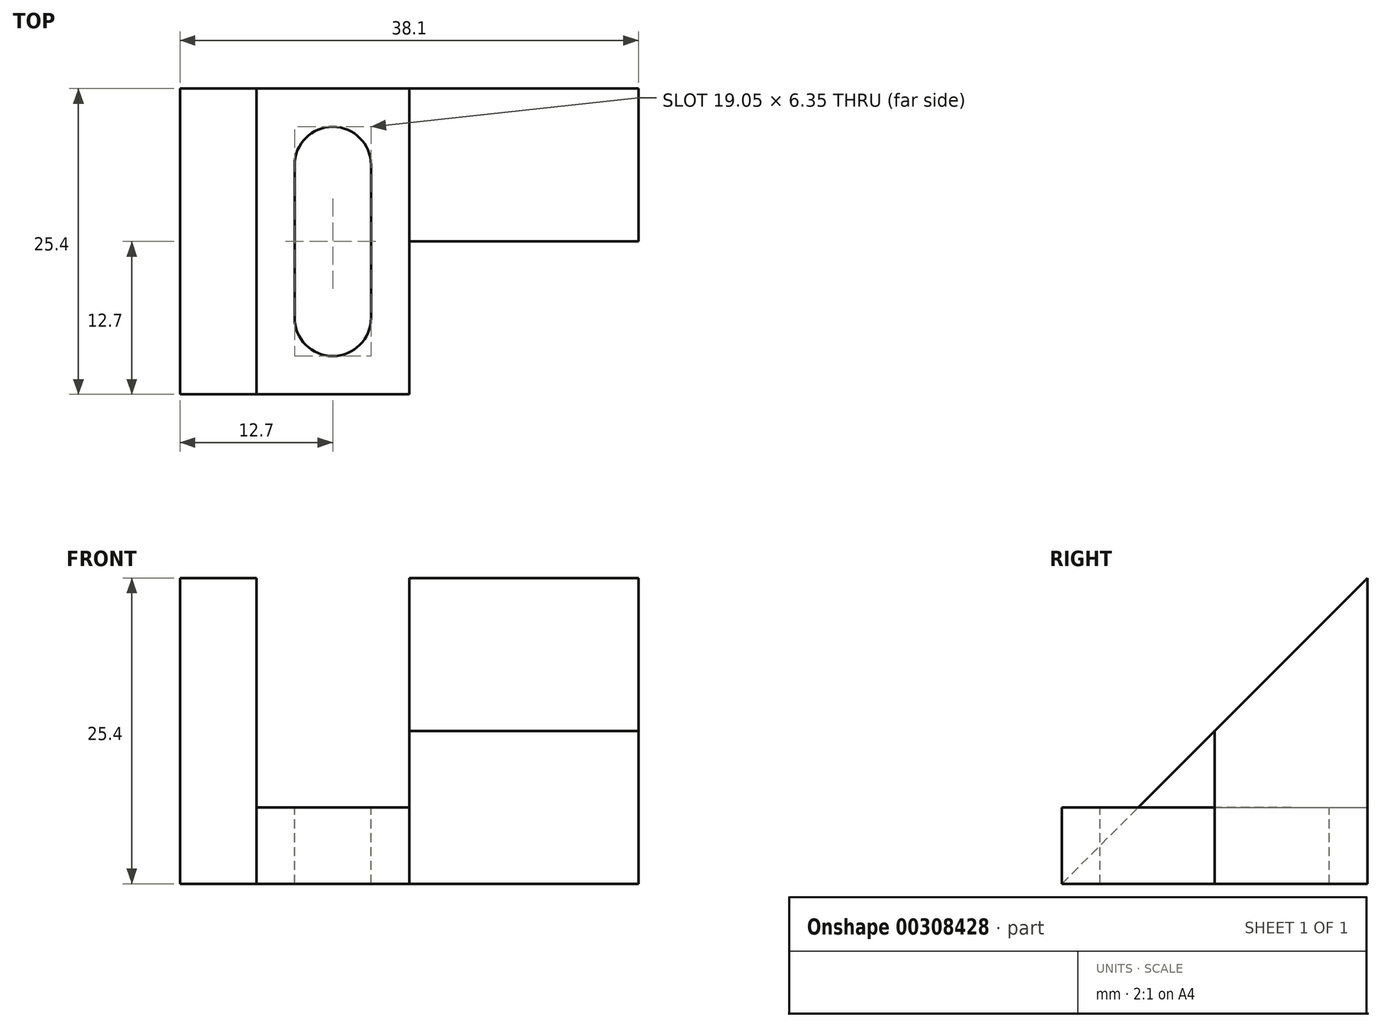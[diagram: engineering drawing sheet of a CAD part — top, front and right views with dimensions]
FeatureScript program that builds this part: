
annotation { "Feature Type Name" : "Feature", "Feature Type Description" : "" }
export const myFeature = defineFeature(function(context is Context, id is Id, definition is map)
    precondition{}
    {
        {
            var Q0;
            Q0=qCreatedBy(makeId("Front.planeOp"),FACE);
            var sketch = newSketch(context, id + "F0", { "sketchPlane" : qUnion([Q0])});
            skLineSegment(sketch, "E0", {"start": v(0, 0) * mm, "end": v(38.1, 0) * mm});
            skLineSegment(sketch, "E1", {"start": v(38.1, 0) * mm, "end": v(38.1, 25.4) * mm});
            skLineSegment(sketch, "E2", {"start": v(38.1, 25.4) * mm, "end": v(19.05, 25.4) * mm});
            skLineSegment(sketch, "E3", {"start": v(19.05, 25.4) * mm, "end": v(19.05, 6.35) * mm});
            skLineSegment(sketch, "E4", {"start": v(19.05, 6.35) * mm, "end": v(6.35, 6.35) * mm});
            skLineSegment(sketch, "E5", {"start": v(6.35, 6.35) * mm, "end": v(6.35, 25.4) * mm});
            skLineSegment(sketch, "E6", {"start": v(6.35, 25.4) * mm, "end": v(0, 25.4) * mm});
            skLineSegment(sketch, "E7", {"start": v(0, 25.4) * mm, "end": v(0, 0) * mm});
            skSolve(sketch);
        }
        {
            var Q0;
            Q0 = qSketchRegion(id + "F0", true);
            extrude(context, id + "F1", {"entities" : qUnion([Q0]), "depth" : 25.4 * mm});
        }
        {
            var Q0;
            Q0=makeQuery(id+"F1.opExtrude","SWEPT_FACE",FACE,{"disambiguationData":[OSD([sQuery(id+"F0.wireOp",EDGE,"E1")])]});
            var sketch = newSketch(context, id + "F2", { "sketchPlane" : qUnion([Q0])});
            skLineSegment(sketch, "E8", {"start": v(-25.4, 0) * mm, "end": v(-12.7, 0) * mm});
            skLineSegment(sketch, "E9", {"start": v(-12.7, 0) * mm, "end": v(-12.7, 25.4) * mm});
            skLineSegment(sketch, "E10", {"start": v(-12.7, 25.4) * mm, "end": v(-25.4, 25.4) * mm});
            skLineSegment(sketch, "E11", {"start": v(-25.4, 25.4) * mm, "end": v(-25.4, 0) * mm});
            skSolve(sketch);
        }
        {
            var Q0;
            Q0 = qSketchRegion(id + "F2", true);
            extrude(context, id + "F3", {"entities" : qUnion([Q0]), "operationType" : NewBodyOperationType.REMOVE, "oppositeDirection" : true, "depth" : 19.05 * mm});
        }
        {
            var Q0;
            Q0=makeQuery(id+"F1.opExtrude","SWEPT_FACE",FACE,{"disambiguationData":[OSD([sQuery(id+"F0.wireOp",EDGE,"E1")])]});
            var sketch = newSketch(context, id + "F4", { "sketchPlane" : qUnion([Q0])});
            skLineSegment(sketch, "E12", {"start": v(-12.7, 12.7) * mm, "end": v(0, 25.4) * mm});
            skLineSegment(sketch, "E13", {"start": v(-12.7, 25.4) * mm, "end": v(-12.7, 12.7) * mm});
            skLineSegment(sketch, "E14", {"start": v(-12.7, 25.4) * mm, "end": v(0, 25.4) * mm});
            skSolve(sketch);
        }
        {
            var Q0;
            Q0 = qSketchRegion(id + "F4", true);
            extrude(context, id + "F5", {"entities" : qUnion([Q0]), "operationType" : NewBodyOperationType.REMOVE, "oppositeDirection" : true, "depth" : 19.05 * mm});
        }
        {
            var Q0;
            Q0=makeQuery(id+"F1.opExtrude","SWEPT_FACE",FACE,{"disambiguationData":[OSD([sQuery(id+"F0.wireOp",EDGE,"E7")])]});
            var sketch = newSketch(context, id + "F6", { "sketchPlane" : qUnion([Q0])});
            skLineSegment(sketch, "E15", {"start": v(0, 25.4) * mm, "end": v(25.4, 25.4) * mm});
            skLineSegment(sketch, "E16", {"start": v(25.4, 25.4) * mm, "end": v(25.4, 0) * mm});
            skLineSegment(sketch, "E17", {"start": v(25.4, 0) * mm, "end": v(0, 25.4) * mm});
            skSolve(sketch);
        }
        {
            var Q0;
            Q0 = qSketchRegion(id + "F6", true);
            extrude(context, id + "F7", {"entities" : qUnion([Q0]), "operationType" : NewBodyOperationType.REMOVE, "oppositeDirection" : true, "depth" : 6.35 * mm});
        }
        {
            var Q0;
            Q0=makeQuery(id+"F1.opExtrude","SWEPT_FACE",FACE,{"disambiguationData":[OSD([sQuery(id+"F0.wireOp",EDGE,"E4")])]});
            var sketch = newSketch(context, id + "F8", { "sketchPlane" : qUnion([Q0])});
            skLineSegment(sketch, "E18", {"start": v(6.35, 0) * mm, "end": v(12.7, 0) * mm});
            skLineSegment(sketch, "E19", {"start": v(12.7, 0) * mm, "end": v(12.7, -6.35) * mm});
            skLineSegment(sketch, "E20", {"start": v(12.7, -25.4) * mm, "end": v(12.7, -19.05) * mm});
            skCircle(sketch, "E21", {"center": v(12.7, -19.05) * mm, "radius": 3.18 * mm});
            skCircle(sketch, "E22", {"center": v(12.7, -6.35) * mm, "radius": 3.18 * mm});
            skLineSegment(sketch, "E23", {"start": v(9.53, -6.35) * mm, "end": v(9.53, -19.05) * mm});
            skLineSegment(sketch, "E24", {"start": v(15.88, -6.35) * mm, "end": v(15.88, -19.05) * mm});
            skSolve(sketch);
        }
        {
            var Q0;
            Q0 = qSketchRegion(id + "F8", true);
            extrude(context, id + "F9", {"entities" : qUnion([Q0]), "operationType" : NewBodyOperationType.REMOVE, "oppositeDirection" : true, "depth" : 25.4 * mm});
        }
    });
